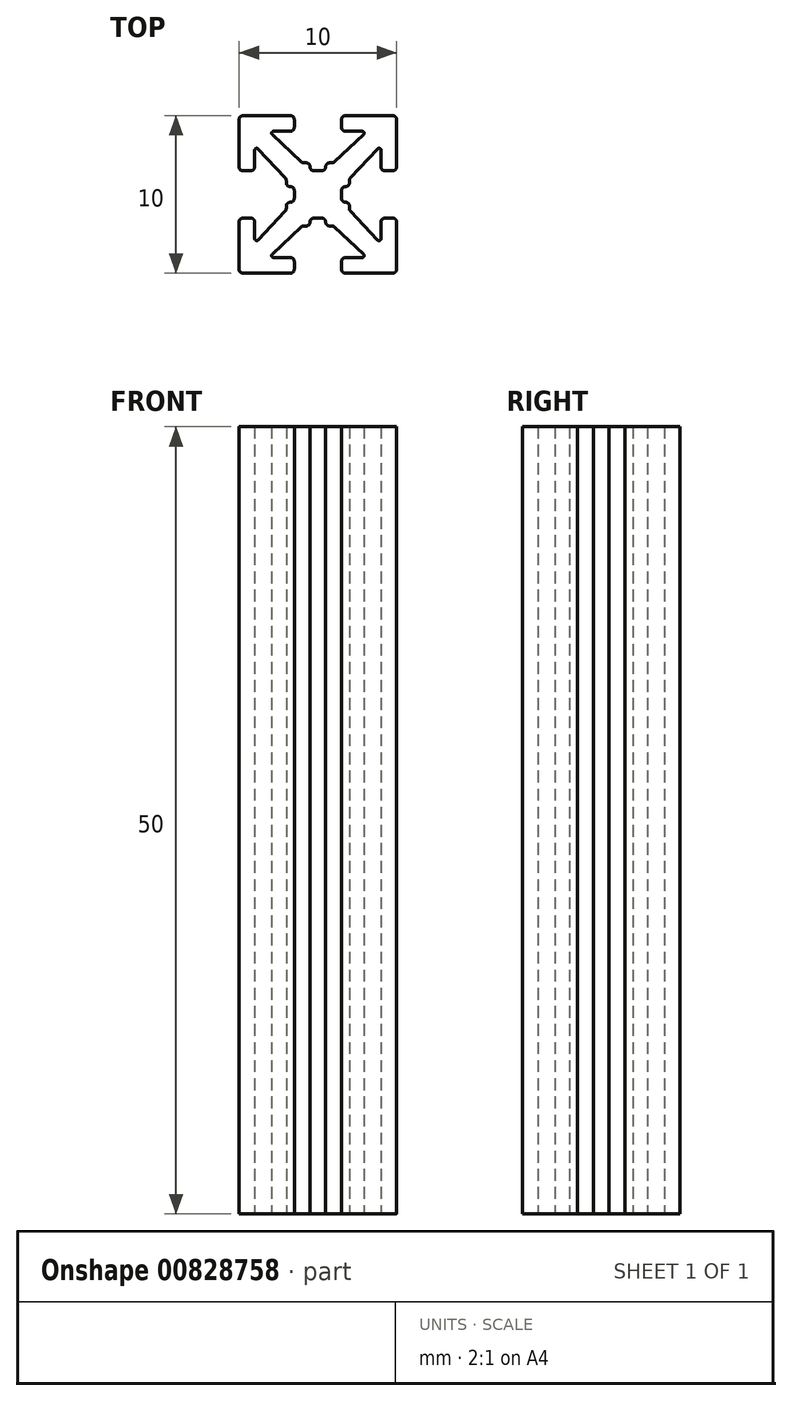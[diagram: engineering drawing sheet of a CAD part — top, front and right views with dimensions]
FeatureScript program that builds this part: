
annotation { "Feature Type Name" : "Feature", "Feature Type Description" : "" }
export const myFeature = defineFeature(function(context is Context, id is Id, definition is map)
    precondition{}
    {
        {
            var Q0;
            Q0=qCreatedBy(makeId("Top.planeOp"),FACE);
            var sketch = newSketch(context, id + "F0", { "sketchPlane" : qUnion([Q0])});
            skArc(sketch, "E0", {"start": v(2.9, 3.8) * mm, "mid": v(2.92, 3.93) * mm, "end": v(2.8, 4.01) * mm});
            skArc(sketch, "E1", {"start": v(0.75, 2) * mm, "mid": v(0.57, 1.93) * mm, "end": v(0.5, 1.75) * mm});
            skArc(sketch, "E2", {"start": v(0.89, 2) * mm, "mid": v(0.98, 2.02) * mm, "end": v(1.06, 2.08) * mm});
            skArc(sketch, "E3", {"start": v(1.5, 4.27) * mm, "mid": v(1.57, 4.09) * mm, "end": v(1.75, 4.01) * mm});
            skArc(sketch, "E4", {"start": v(1.75, 5) * mm, "mid": v(1.57, 4.93) * mm, "end": v(1.5, 4.75) * mm});
            skArc(sketch, "E5", {"start": v(0.24, 1.5) * mm, "mid": v(0.42, 1.57) * mm, "end": v(0.5, 1.75) * mm});
            skArc(sketch, "E6", {"start": v(4.75, 1.5) * mm, "mid": v(4.93, 1.57) * mm, "end": v(5, 1.75) * mm});
            skArc(sketch, "E7", {"start": v(4.01, 1.75) * mm, "mid": v(4.09, 1.57) * mm, "end": v(4.27, 1.5) * mm});
            skArc(sketch, "E8", {"start": v(4.01, 2.8) * mm, "mid": v(3.93, 2.92) * mm, "end": v(3.8, 2.9) * mm});
            skArc(sketch, "E9", {"start": v(2.08, 1.06) * mm, "mid": v(2.02, 0.98) * mm, "end": v(2, 0.89) * mm});
            skArc(sketch, "E10", {"start": v(1.75, 0.5) * mm, "mid": v(1.93, 0.57) * mm, "end": v(2, 0.75) * mm});
            skArc(sketch, "E11", {"start": v(1.75, 0.5) * mm, "mid": v(1.57, 0.42) * mm, "end": v(1.5, 0.24) * mm});
            skArc(sketch, "E12", {"start": v(0.5, -1.75) * mm, "mid": v(0.42, -1.57) * mm, "end": v(0.24, -1.5) * mm});
            skArc(sketch, "E13", {"start": v(0.5, -1.75) * mm, "mid": v(0.57, -1.93) * mm, "end": v(0.75, -2) * mm});
            skArc(sketch, "E14", {"start": v(1.06, -2.08) * mm, "mid": v(0.98, -2.02) * mm, "end": v(0.89, -2) * mm});
            skArc(sketch, "E15", {"start": v(2.8, -4.01) * mm, "mid": v(2.92, -3.93) * mm, "end": v(2.9, -3.8) * mm});
            skArc(sketch, "E16", {"start": v(1.75, -4.01) * mm, "mid": v(1.57, -4.09) * mm, "end": v(1.5, -4.27) * mm});
            skArc(sketch, "E17", {"start": v(1.5, -4.75) * mm, "mid": v(1.57, -4.93) * mm, "end": v(1.75, -5) * mm});
            skArc(sketch, "E18", {"start": v(5, -1.75) * mm, "mid": v(4.93, -1.57) * mm, "end": v(4.75, -1.5) * mm});
            skArc(sketch, "E19", {"start": v(4.27, -1.5) * mm, "mid": v(4.09, -1.57) * mm, "end": v(4.01, -1.75) * mm});
            skArc(sketch, "E20", {"start": v(3.8, -2.9) * mm, "mid": v(3.93, -2.92) * mm, "end": v(4.01, -2.8) * mm});
            skArc(sketch, "E21", {"start": v(2, -0.89) * mm, "mid": v(2.02, -0.98) * mm, "end": v(2.08, -1.06) * mm});
            skArc(sketch, "E22", {"start": v(2, -0.75) * mm, "mid": v(1.93, -0.57) * mm, "end": v(1.75, -0.5) * mm});
            skArc(sketch, "E23", {"start": v(1.5, -0.24) * mm, "mid": v(1.57, -0.42) * mm, "end": v(1.75, -0.5) * mm});
            skArc(sketch, "E24", {"start": v(-0.5, 1.75) * mm, "mid": v(-0.42, 1.57) * mm, "end": v(-0.24, 1.5) * mm});
            skArc(sketch, "E25", {"start": v(-0.5, 1.75) * mm, "mid": v(-0.57, 1.93) * mm, "end": v(-0.75, 2) * mm});
            skArc(sketch, "E26", {"start": v(-1.06, 2.08) * mm, "mid": v(-0.98, 2.02) * mm, "end": v(-0.89, 2) * mm});
            skArc(sketch, "E27", {"start": v(-2.8, 4.01) * mm, "mid": v(-2.92, 3.93) * mm, "end": v(-2.9, 3.8) * mm});
            skArc(sketch, "E28", {"start": v(-1.75, 4.01) * mm, "mid": v(-1.57, 4.09) * mm, "end": v(-1.5, 4.27) * mm});
            skArc(sketch, "E29", {"start": v(-1.5, 4.75) * mm, "mid": v(-1.57, 4.93) * mm, "end": v(-1.75, 5) * mm});
            skArc(sketch, "E30", {"start": v(-5, 1.75) * mm, "mid": v(-4.93, 1.57) * mm, "end": v(-4.75, 1.5) * mm});
            skArc(sketch, "E31", {"start": v(-4.27, 1.5) * mm, "mid": v(-4.09, 1.57) * mm, "end": v(-4.01, 1.75) * mm});
            skArc(sketch, "E32", {"start": v(-3.8, 2.9) * mm, "mid": v(-3.93, 2.92) * mm, "end": v(-4.01, 2.8) * mm});
            skArc(sketch, "E33", {"start": v(-2, 0.89) * mm, "mid": v(-2.02, 0.98) * mm, "end": v(-2.08, 1.06) * mm});
            skArc(sketch, "E34", {"start": v(-2, 0.75) * mm, "mid": v(-1.93, 0.57) * mm, "end": v(-1.75, 0.5) * mm});
            skArc(sketch, "E35", {"start": v(-1.5, 0.24) * mm, "mid": v(-1.57, 0.42) * mm, "end": v(-1.75, 0.5) * mm});
            skArc(sketch, "E36", {"start": v(-1.75, -0.5) * mm, "mid": v(-1.57, -0.42) * mm, "end": v(-1.5, -0.24) * mm});
            skArc(sketch, "E37", {"start": v(-1.75, -0.5) * mm, "mid": v(-1.93, -0.57) * mm, "end": v(-2, -0.75) * mm});
            skArc(sketch, "E38", {"start": v(-2.08, -1.06) * mm, "mid": v(-2.02, -0.98) * mm, "end": v(-2, -0.89) * mm});
            skArc(sketch, "E39", {"start": v(-4.01, -2.8) * mm, "mid": v(-3.93, -2.92) * mm, "end": v(-3.8, -2.9) * mm});
            skArc(sketch, "E40", {"start": v(-4.01, -1.75) * mm, "mid": v(-4.09, -1.57) * mm, "end": v(-4.27, -1.5) * mm});
            skArc(sketch, "E41", {"start": v(-4.75, -1.5) * mm, "mid": v(-4.93, -1.57) * mm, "end": v(-5, -1.75) * mm});
            skArc(sketch, "E42", {"start": v(-1.75, -5) * mm, "mid": v(-1.57, -4.93) * mm, "end": v(-1.5, -4.75) * mm});
            skArc(sketch, "E43", {"start": v(-1.5, -4.27) * mm, "mid": v(-1.57, -4.09) * mm, "end": v(-1.75, -4.01) * mm});
            skArc(sketch, "E44", {"start": v(-2.9, -3.8) * mm, "mid": v(-2.92, -3.93) * mm, "end": v(-2.8, -4.01) * mm});
            skArc(sketch, "E45", {"start": v(-0.89, -2) * mm, "mid": v(-0.98, -2.02) * mm, "end": v(-1.06, -2.08) * mm});
            skArc(sketch, "E46", {"start": v(-0.75, -2) * mm, "mid": v(-0.57, -1.93) * mm, "end": v(-0.5, -1.75) * mm});
            skArc(sketch, "E47", {"start": v(-0.24, -1.5) * mm, "mid": v(-0.42, -1.57) * mm, "end": v(-0.5, -1.75) * mm});
            skArc(sketch, "E48", {"start": v(-4.75, 5) * mm, "mid": v(-4.93, 4.93) * mm, "end": v(-5, 4.75) * mm});
            skArc(sketch, "E49", {"start": v(-5, -4.75) * mm, "mid": v(-4.93, -4.93) * mm, "end": v(-4.75, -5) * mm});
            skArc(sketch, "E50", {"start": v(4.75, -5) * mm, "mid": v(4.93, -4.93) * mm, "end": v(5, -4.75) * mm});
            skArc(sketch, "E51", {"start": v(5, 4.75) * mm, "mid": v(4.93, 4.93) * mm, "end": v(4.75, 5) * mm});
            skLineSegment(sketch, "E52", {"start": v(-0.24, 1.5) * mm, "end": v(0.24, 1.5) * mm});
            skLineSegment(sketch, "E53", {"start": v(5, 1.75) * mm, "end": v(5, 4.75) * mm});
            skLineSegment(sketch, "E54", {"start": v(0.75, 2) * mm, "end": v(0.89, 2) * mm});
            skLineSegment(sketch, "E55", {"start": v(1.06, 2.08) * mm, "end": v(2.9, 3.8) * mm});
            skLineSegment(sketch, "E56", {"start": v(2.8, 4.01) * mm, "end": v(1.75, 4.01) * mm});
            skLineSegment(sketch, "E57", {"start": v(1.5, 4.27) * mm, "end": v(1.5, 4.75) * mm});
            skLineSegment(sketch, "E58", {"start": v(1.75, 5) * mm, "end": v(4.75, 5) * mm});
            skLineSegment(sketch, "E59", {"start": v(4.27, 1.5) * mm, "end": v(4.75, 1.5) * mm});
            skLineSegment(sketch, "E60", {"start": v(4.01, 2.8) * mm, "end": v(4.01, 1.75) * mm});
            skLineSegment(sketch, "E61", {"start": v(2.08, 1.06) * mm, "end": v(3.8, 2.9) * mm});
            skLineSegment(sketch, "E62", {"start": v(2, 0.75) * mm, "end": v(2, 0.89) * mm});
            skLineSegment(sketch, "E63", {"start": v(1.5, -0.24) * mm, "end": v(1.5, 0.24) * mm});
            skLineSegment(sketch, "E64", {"start": v(-0.24, -1.5) * mm, "end": v(0.24, -1.5) * mm});
            skLineSegment(sketch, "E65", {"start": v(0.75, -2) * mm, "end": v(0.89, -2) * mm});
            skLineSegment(sketch, "E66", {"start": v(1.06, -2.08) * mm, "end": v(2.9, -3.8) * mm});
            skLineSegment(sketch, "E67", {"start": v(2.8, -4.01) * mm, "end": v(1.75, -4.01) * mm});
            skLineSegment(sketch, "E68", {"start": v(1.5, -4.27) * mm, "end": v(1.5, -4.75) * mm});
            skLineSegment(sketch, "E69", {"start": v(1.75, -5) * mm, "end": v(4.75, -5) * mm});
            skLineSegment(sketch, "E70", {"start": v(5, -1.75) * mm, "end": v(5, -4.75) * mm});
            skLineSegment(sketch, "E71", {"start": v(4.27, -1.5) * mm, "end": v(4.75, -1.5) * mm});
            skLineSegment(sketch, "E72", {"start": v(4.01, -2.8) * mm, "end": v(4.01, -1.75) * mm});
            skLineSegment(sketch, "E73", {"start": v(2.08, -1.06) * mm, "end": v(3.8, -2.9) * mm});
            skLineSegment(sketch, "E74", {"start": v(2, -0.75) * mm, "end": v(2, -0.89) * mm});
            skLineSegment(sketch, "E75", {"start": v(-0.75, 2) * mm, "end": v(-0.89, 2) * mm});
            skLineSegment(sketch, "E76", {"start": v(-1.06, 2.08) * mm, "end": v(-2.9, 3.8) * mm});
            skLineSegment(sketch, "E77", {"start": v(-2.8, 4.01) * mm, "end": v(-1.75, 4.01) * mm});
            skLineSegment(sketch, "E78", {"start": v(-1.5, 4.27) * mm, "end": v(-1.5, 4.75) * mm});
            skLineSegment(sketch, "E79", {"start": v(-1.75, 5) * mm, "end": v(-4.75, 5) * mm});
            skLineSegment(sketch, "E80", {"start": v(-5, 1.75) * mm, "end": v(-5, 4.75) * mm});
            skLineSegment(sketch, "E81", {"start": v(-4.27, 1.5) * mm, "end": v(-4.75, 1.5) * mm});
            skLineSegment(sketch, "E82", {"start": v(-4.01, 2.8) * mm, "end": v(-4.01, 1.75) * mm});
            skLineSegment(sketch, "E83", {"start": v(-2.08, 1.06) * mm, "end": v(-3.8, 2.9) * mm});
            skLineSegment(sketch, "E84", {"start": v(-2, 0.75) * mm, "end": v(-2, 0.89) * mm});
            skLineSegment(sketch, "E85", {"start": v(-1.5, -0.24) * mm, "end": v(-1.5, 0.24) * mm});
            skLineSegment(sketch, "E86", {"start": v(-2, -0.75) * mm, "end": v(-2, -0.89) * mm});
            skLineSegment(sketch, "E87", {"start": v(-2.08, -1.06) * mm, "end": v(-3.8, -2.9) * mm});
            skLineSegment(sketch, "E88", {"start": v(-4.01, -2.8) * mm, "end": v(-4.01, -1.75) * mm});
            skLineSegment(sketch, "E89", {"start": v(-4.27, -1.5) * mm, "end": v(-4.75, -1.5) * mm});
            skLineSegment(sketch, "E90", {"start": v(-5, -1.75) * mm, "end": v(-5, -4.75) * mm});
            skLineSegment(sketch, "E91", {"start": v(-1.75, -5) * mm, "end": v(-4.75, -5) * mm});
            skLineSegment(sketch, "E92", {"start": v(-1.5, -4.27) * mm, "end": v(-1.5, -4.75) * mm});
            skLineSegment(sketch, "E93", {"start": v(-2.8, -4.01) * mm, "end": v(-1.75, -4.01) * mm});
            skLineSegment(sketch, "E94", {"start": v(-1.06, -2.08) * mm, "end": v(-2.9, -3.8) * mm});
            skLineSegment(sketch, "E95", {"start": v(-0.75, -2) * mm, "end": v(-0.89, -2) * mm});
            skSolve(sketch);
        }
        {
            var Q0;
            Q0=makeQuery(id+"F0.imprint","IMPRINT",FACE,{"disambiguationData":[TD([[makeQuery(id+"F0.imprint","IMPRINT",EDGE,{"derivedFrom":sQuery(id+"F0.wireOp",EDGE,"E0")}),-1.0]])]});
            extrude(context, id + "F1", {"entities" : qUnion([Q0]), "endBound" : BoundingType.SYMMETRIC, "depth" : 50 * mm, "offsetDistance" : 25 * mm});
        }
    });
